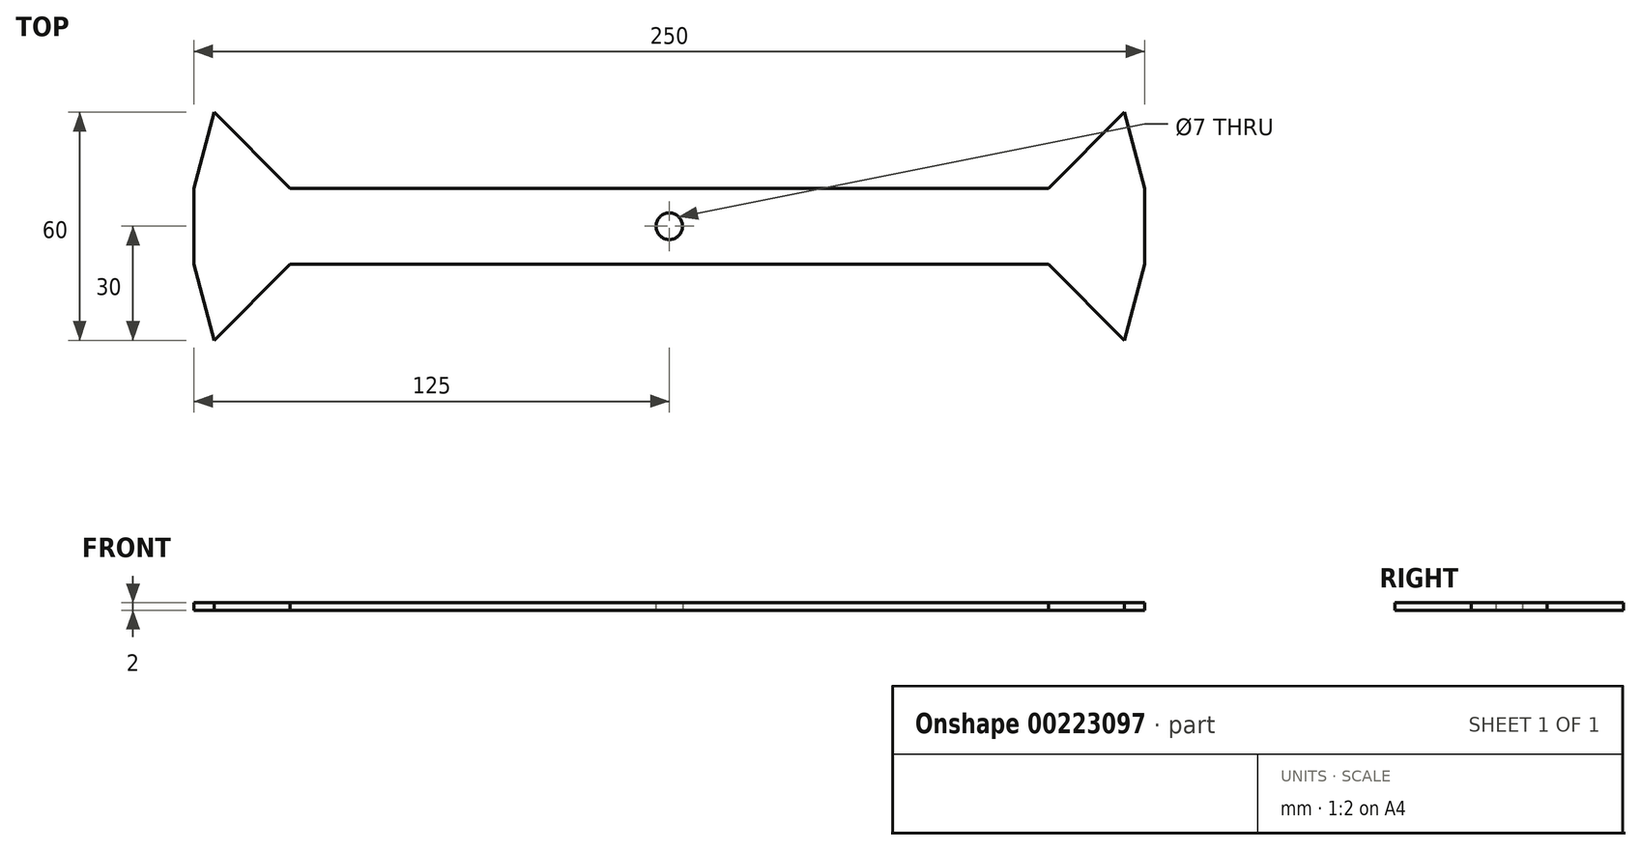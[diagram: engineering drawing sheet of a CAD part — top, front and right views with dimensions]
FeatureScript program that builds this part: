
annotation { "Feature Type Name" : "Feature", "Feature Type Description" : "" }
export const myFeature = defineFeature(function(context is Context, id is Id, definition is map)
    precondition{}
    {
        {
            var Q0;
            Q0=qCreatedBy(makeId("Top.planeOp"),FACE);
            var sketch = newSketch(context, id + "F0", { "sketchPlane" : qUnion([Q0])});
            skCircle(sketch, "E0", {"center": v(0, 0) * mm, "radius": 3.5 * mm});
            skLineSegment(sketch, "E1.bottom", {"start": v(125, 10) * mm, "end": v(-125, 10) * mm});
            skLineSegment(sketch, "E1.top", {"start": v(125, -10) * mm, "end": v(-125, -10) * mm});
            skLineSegment(sketch, "E1.left", {"start": v(125, 10) * mm, "end": v(125, -10) * mm});
            skLineSegment(sketch, "E1.right", {"start": v(-125, 10) * mm, "end": v(-125, -10) * mm});
            skLineSegment(sketch, "E2", {"start": v(-125, -10) * mm, "end": v(-119.64, -30) * mm});
            skLineSegment(sketch, "E3", {"start": v(-119.64, -30) * mm, "end": v(-99.64, -10) * mm});
            skLineSegment(sketch, "E4", {"start": v(0, 0) * mm, "end": v(-125, 0) * mm, "construction": true});
            skLineSegment(sketch, "E5.MirrorCS", {"start": v(-119.64, 30) * mm, "end": v(-99.64, 10) * mm});
            skLineSegment(sketch, "E6.MirrorCS", {"start": v(-125, 10) * mm, "end": v(-119.64, 30) * mm});
            skLineSegment(sketch, "E7", {"start": v(0, 0) * mm, "end": v(0, 27.6) * mm, "construction": true});
            skLineSegment(sketch, "E8.MirrorCS", {"start": v(119.64, -30) * mm, "end": v(99.64, -10) * mm});
            skLineSegment(sketch, "E9.MirrorCS", {"start": v(125, -10) * mm, "end": v(119.64, -30) * mm});
            skLineSegment(sketch, "E10.MirrorCS", {"start": v(119.64, 30) * mm, "end": v(99.64, 10) * mm});
            skLineSegment(sketch, "E11.MirrorCS", {"start": v(125, 10) * mm, "end": v(119.64, 30) * mm});
            skSolve(sketch);
        }
        {
            var Q0;
            Q0 = qSketchRegion(id + "F0", true);
            extrude(context, id + "F1", {"entities" : qUnion([Q0]), "depth" : 2 * mm, "offsetDistance" : 25 * mm});
        }
    });
